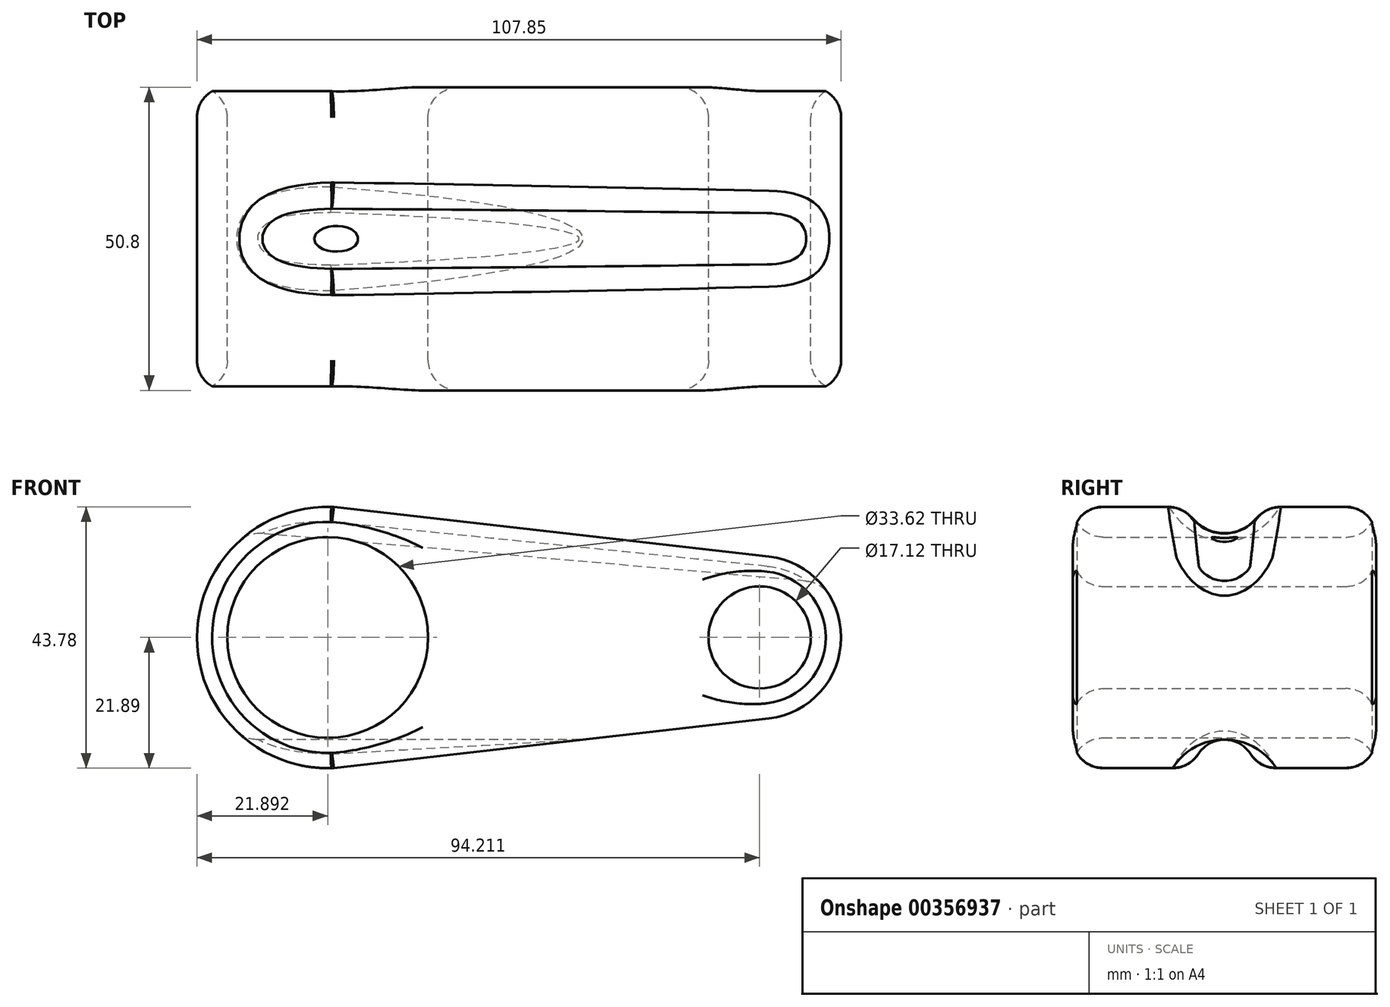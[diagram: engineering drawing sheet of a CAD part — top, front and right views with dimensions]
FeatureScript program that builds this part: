
annotation { "Feature Type Name" : "Feature", "Feature Type Description" : "" }
export const myFeature = defineFeature(function(context is Context, id is Id, definition is map)
    precondition{}
    {
        {
            var Q0;
            Q0=qCreatedBy(makeId("Front.planeOp"),FACE);
            var sketch = newSketch(context, id + "F0", { "sketchPlane" : qUnion([Q0])});
            skArc(sketch, "E0", {"start": v(-39.77, 21.5) * mm, "mid": v(-65.79, 0) * mm, "end": v(-39.77, -21.5) * mm});
            skArc(sketch, "E1", {"start": v(29.97, -13.55) * mm, "mid": v(42.06, 0) * mm, "end": v(29.97, 13.55) * mm});
            skLineSegment(sketch, "E2", {"start": v(-43.08, 21.88) * mm, "end": v(29.97, 13.55) * mm});
            skLineSegment(sketch, "E3", {"start": v(29.97, -13.55) * mm, "end": v(-43.08, -21.88) * mm});
            skCircle(sketch, "E4", {"center": v(-43.9, 0) * mm, "radius": 16.81 * mm});
            skCircle(sketch, "E5", {"center": v(28.42, 0) * mm, "radius": 8.56 * mm});
            skSolve(sketch);
        }
        {
            var Q0;
            {var subQ3=sQuery(id+"F0.wireOp",EDGE,"E1");Q0=makeQuery(id+"F0.imprint","IMPRINT",FACE,{"disambiguationData":[TD([[makeQuery(id+"F0.imprint","IMPRINT",EDGE,{"derivedFrom":subQ3}),1.0]])]});}
            extrude(context, id + "F1", {"entities" : qUnion([Q0]), "depth" : 25.4 * mm});
        }
        {
            var Q0;
            Q0=makeQuery(id+"F1.opExtrude","CAP_FACE",FACE,{"disambiguationData":[OSD([sQuery(id+"F0.wireOp",EDGE,"E0"),sQuery(id+"F0.wireOp",EDGE,"E1"),sQuery(id+"F0.wireOp",EDGE,"E2"),sQuery(id+"F0.wireOp",EDGE,"E3"),sQuery(id+"F0.wireOp",EDGE,"E4"),sQuery(id+"F0.wireOp",EDGE,"E5")])],"isStart":false});
            fillet(context, id + "F2", {"entities" : qUnion([Q0]), "radius" : 5.08 * mm, "tangentPropagation" : true, "allowEdgeOverflow" : false});
        }
        {
            var Q0;
            Q0=makeQuery(id+"F1.opExtrude","SWEPT_BODY",BODY,{"disambiguationData":[OSD([sQuery(id+"F0.wireOp",EDGE,"E0"),sQuery(id+"F0.wireOp",EDGE,"E1"),sQuery(id+"F0.wireOp",EDGE,"E2"),sQuery(id+"F0.wireOp",EDGE,"E3"),sQuery(id+"F0.wireOp",EDGE,"E4"),sQuery(id+"F0.wireOp",EDGE,"E5")])]});
            var Q1;
            Q1=qCreatedBy(makeId("Front.planeOp"),FACE);
            mirror(context, id + "F3", {"operationType" : NewBodyOperationType.ADD, "entities" : qUnion([Q0]), "mirrorPlane" : qUnion([Q1])});
        }
        {
            var Q0;
            {var subQ0=makeQuery(id+"F1.opExtrude","SWEPT_EDGE",EDGE,{"disambiguationData":[OSD([sQuery(id+"F0.wireOp",EDGE,"E0"),sQuery(id+"F0.wireOp",EDGE,"E2")])]});Q0=makeQuery(id+"F3.boolean.opBoolean","MERGE",EDGE,{"derivedFrom":[subQ0,makeQuery(id+"F3.opPattern","COPY",EDGE,{"derivedFrom":subQ0,"instanceName":"1"})]});}
            cPlane(context, id + "F4", {"entities" : qUnion([Q0]), "cplaneType" : CPlaneType.LINE_ANGLE, "offset" : 25.4 * mm, "angle" : 95 * degree, "width" : 152.4 * mm, "height" : 152.4 * mm});
        }
        {
            var Q0;
            Q0=qCreatedBy(id+"F4.planeOp",FACE);
            var sketch = newSketch(context, id + "F5", { "sketchPlane" : qUnion([Q0])});
            skCircle(sketch, "E6", {"center": v(0, 18.39) * mm, "radius": 5.82 * mm});
            skSolve(sketch);
        }
        {
            var Q0;
            Q0=makeQuery(id+"F5.imprint","IMPRINT",FACE,{"disambiguationData":[TD([[makeQuery(id+"F5.imprint","IMPRINT",EDGE,{"derivedFrom":sQuery(id+"F5.wireOp",EDGE,"E6")}),1.0]])]});
            extrude(context, id + "F6", {"entities" : qUnion([Q0]), "operationType" : NewBodyOperationType.REMOVE, "oppositeDirection" : true, "depth" : -101.6 * mm, "hasSecondDirection" : true, "secondDirectionOppositeDirection" : false, "secondDirectionDepth" : -127 * mm});
        }
        {
            var Q0;
            {var subQ1=sQuery(id+"F0.wireOp",EDGE,"E0");var subQ4=sQuery(id+"F0.wireOp",EDGE,"E2");var subQ5=makeQuery(id+"F1.opExtrude","SWEPT_FACE",FACE,{"disambiguationData":[OSD([subQ4])]});Q0=makeQuery(id+"F6.boolean.opBoolean","SPLIT",FACE,{"disambiguationData":[TD([makeQuery(id+"F3.opPattern","COPY",FACE,{"derivedFrom":makeQuery(id+"F2.opFillet","BLEND_FACE",FACE,{"disambiguationData":[OSD([subQ1])]}),"instanceName":"1"})])],"derivedFrom":makeQuery(id+"F3.boolean.opBoolean","MERGE",FACE,{"derivedFrom":[subQ5,makeQuery(id+"F3.opPattern","COPY",FACE,{"derivedFrom":subQ5,"instanceName":"1"})]})});}
            var Q1;
            {var subQ0=makeQuery(id+"F1.opExtrude","SWEPT_FACE",FACE,{"disambiguationData":[OSD([sQuery(id+"F0.wireOp",EDGE,"E0")])]});Q1=makeQuery(id+"F3.boolean.opBoolean","MERGE",FACE,{"derivedFrom":[subQ0,makeQuery(id+"F3.opPattern","COPY",FACE,{"derivedFrom":subQ0,"instanceName":"1"})]});}
            var Q2;
            {var subQ1=sQuery(id+"F0.wireOp",EDGE,"E0");var subQ4=sQuery(id+"F0.wireOp",EDGE,"E2");var subQ5=makeQuery(id+"F1.opExtrude","SWEPT_FACE",FACE,{"disambiguationData":[OSD([subQ4])]});Q2=makeQuery(id+"F6.boolean.opBoolean","SPLIT",FACE,{"disambiguationData":[TD([makeQuery(id+"F2.opFillet","BLEND_FACE",FACE,{"disambiguationData":[OSD([subQ1])]})])],"derivedFrom":makeQuery(id+"F3.boolean.opBoolean","MERGE",FACE,{"derivedFrom":[subQ5,makeQuery(id+"F3.opPattern","COPY",FACE,{"derivedFrom":subQ5,"instanceName":"1"})]})});}
            var Q3;
            {var subQ0=makeQuery(id+"F1.opExtrude","SWEPT_FACE",FACE,{"disambiguationData":[OSD([sQuery(id+"F0.wireOp",EDGE,"E1")])]});Q3=makeQuery(id+"F3.boolean.opBoolean","MERGE",FACE,{"derivedFrom":[subQ0,makeQuery(id+"F3.opPattern","COPY",FACE,{"derivedFrom":subQ0,"instanceName":"1"})]});}
            fillet(context, id + "F7", {"entities" : qUnion([Q0, Q1, Q2, Q3]), "radius" : 5.08 * mm, "tangentPropagation" : true, "allowEdgeOverflow" : false});
        }
        {
            var Q0;
            Q0=qCreatedBy(makeId("Right.planeOp"),FACE);
            var sketch = newSketch(context, id + "F8", { "sketchPlane" : qUnion([Q0])});
            skCircle(sketch, "E7", {"center": v(0, -22.32) * mm, "radius": 5.2 * mm});
            skSolve(sketch);
        }
        {
            var Q0;
            Q0=makeQuery(id+"F8.imprint","IMPRINT",FACE,{"disambiguationData":[TD([[makeQuery(id+"F8.imprint","IMPRINT",EDGE,{"derivedFrom":sQuery(id+"F8.wireOp",EDGE,"E7")}),1.0]])]});
            extrude(context, id + "F9", {"entities" : qUnion([Q0]), "operationType" : NewBodyOperationType.REMOVE, "depth" : 101.6 * mm, "hasSecondDirection" : true, "secondDirectionOppositeDirection" : true, "secondDirectionDepth" : 101.6 * mm});
        }
        {
            var Q0;
            {var subQ0=makeQuery(id+"F1.opExtrude","SWEPT_FACE",FACE,{"disambiguationData":[OSD([sQuery(id+"F0.wireOp",EDGE,"E3")])]});Q0=makeQuery(id+"F3.boolean.opBoolean","MERGE",FACE,{"derivedFrom":[subQ0,makeQuery(id+"F3.opPattern","COPY",FACE,{"derivedFrom":subQ0,"instanceName":"1"})]});}
            fillet(context, id + "F10", {"entities" : qUnion([Q0]), "radius" : 5.08 * mm, "tangentPropagation" : true, "allowEdgeOverflow" : false});
        }
    });
